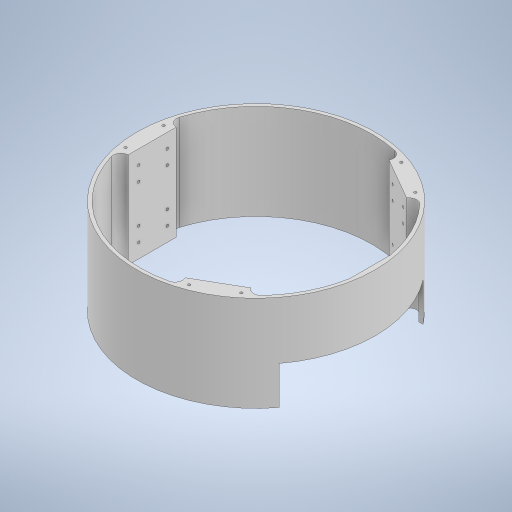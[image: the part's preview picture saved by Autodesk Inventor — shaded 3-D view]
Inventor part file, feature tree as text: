
AUTODESK INVENTOR PART (.ipt)
format: ipt  version: 2023 (Build 270158000, 158)  size: 378,880 bytes
history: native  units: mm
features: sketch x9, hole x5, extrude x4, other x1, fillet x1
ambient origin geometry x8: Origin, YZ Plane, XZ Plane, XY Plane, X Axis, Y Axis, Z Axis, Center Point
bodies: Body1 (feature_tree)
feature tree (20):
  other  "ソリッド1"
  extrude  "押し出し1"  Depth=250.0mm
  fillet  "フィレット1"  Radius=243.0mm
  extrude  "押し出し4"  Depth=118.86mm
  extrude  "押し出し5"  Depth=10.0mm
  extrude  "押し出し6"  Depth=30.0mm TaperAngle=360.0deg
  hole  "穴1"  [1 undecoded]
  hole  "穴2"  [1 undecoded]
  hole  "穴3"  [1 undecoded]
  hole  "穴4"  [1 undecoded]
  hole  "穴5"  [1 undecoded]
  sketch  "スケッチ1"
  sketch  "スケッチ4"
  sketch  "スケッチ5"
  sketch  "スケッチ6"
  sketch  "スケッチ7"
  sketch  "スケッチ8"
  sketch  "スケッチ9"
  sketch  "スケッチ10"
  sketch  "スケッチ11"
note: 5 required parameter values undecoded (feature->parameter linkage not recoverable at this tier; creation-order binding heuristic only, values carry confidence <= 0.55)
